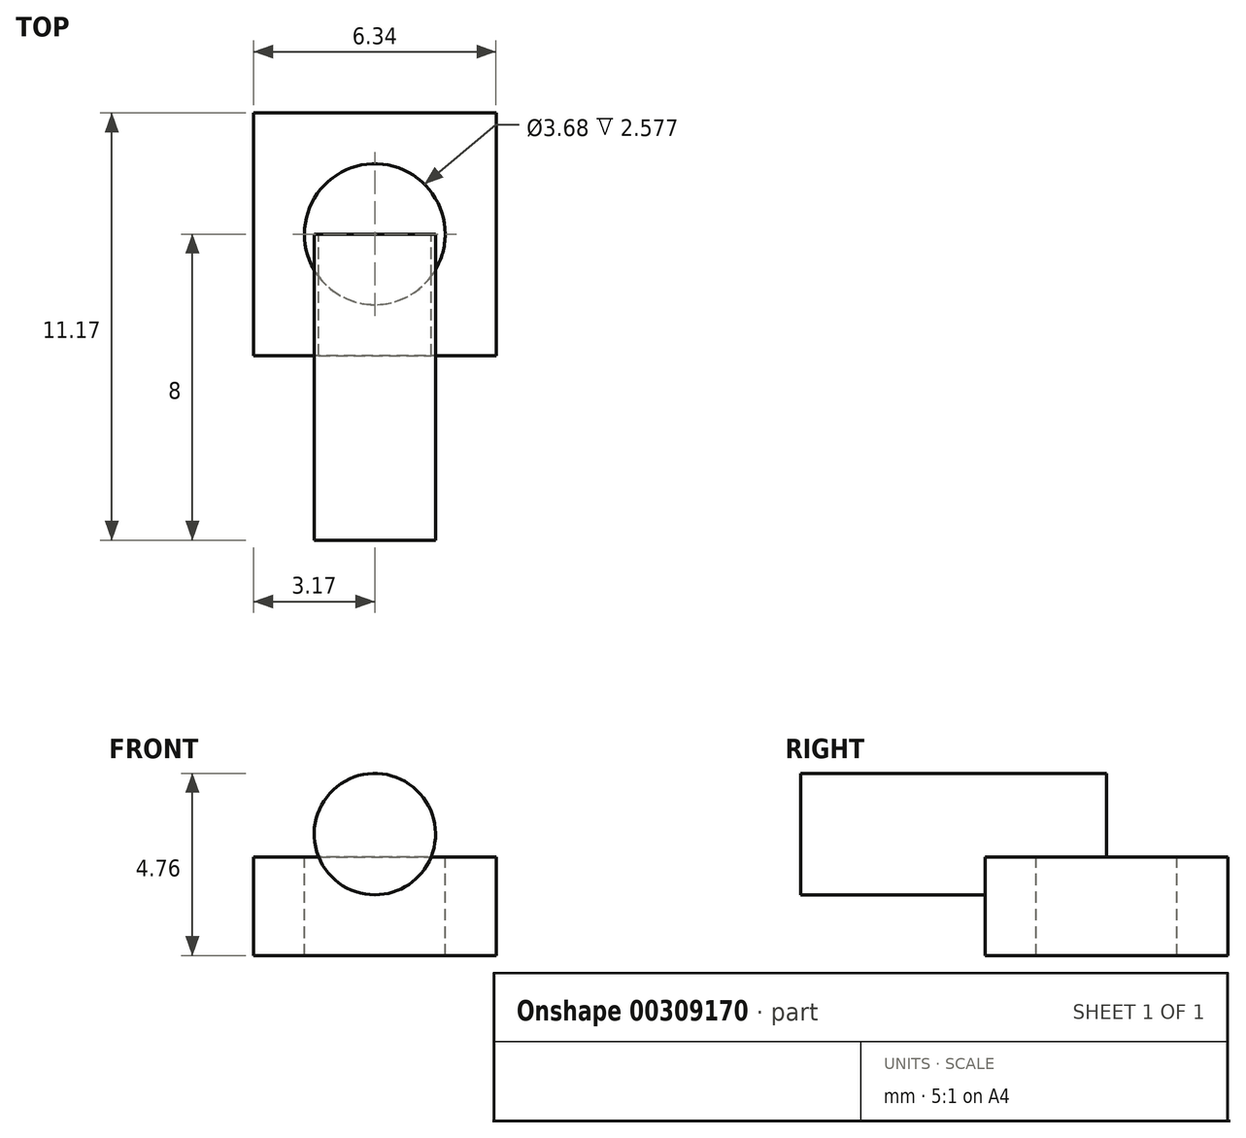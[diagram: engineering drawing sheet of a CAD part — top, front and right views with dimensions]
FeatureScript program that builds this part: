
annotation { "Feature Type Name" : "Feature", "Feature Type Description" : "" }
export const myFeature = defineFeature(function(context is Context, id is Id, definition is map)
    precondition{}
    {
        {
            var Q0;
            Q0=qCreatedBy(makeId("Front.planeOp"),FACE);
            var sketch = newSketch(context, id + "F0", { "sketchPlane" : qUnion([Q0])});
            skLineSegment(sketch, "E0", {"start": v(0, 0) * mm, "end": v(0, 3.18) * mm, "construction": true});
            skCircle(sketch, "E1", {"center": v(0, 3.18) * mm, "radius": 1.59 * mm});
            skSolve(sketch);
        }
        {
            var Q0;
            Q0=qCreatedBy(makeId("Top.planeOp"),FACE);
            var sketch = newSketch(context, id + "F1", { "sketchPlane" : qUnion([Q0])});
            skLineSegment(sketch, "E2.bottom", {"start": v(3.17, -3.18) * mm, "end": v(-3.18, -3.18) * mm});
            skLineSegment(sketch, "E2.top", {"start": v(3.17, 3.18) * mm, "end": v(-3.18, 3.18) * mm});
            skLineSegment(sketch, "E2.left", {"start": v(3.17, -3.18) * mm, "end": v(3.17, 3.17) * mm});
            skLineSegment(sketch, "E2.right", {"start": v(-3.18, -3.18) * mm, "end": v(-3.18, 3.17) * mm});
            skPoint(sketch, "E2.middle", {"position": v(0, 0) * mm});
            skCircle(sketch, "E3", {"center": v(0, 0) * mm, "radius": 1.59 * mm});
            skSolve(sketch);
        }
        {
            var Q0;
            Q0=makeQuery(id+"F1.imprint","IMPRINT",FACE,{"disambiguationData":[TD([[makeQuery(id+"F1.imprint","IMPRINT",EDGE,{"derivedFrom":sQuery(id+"F1.wireOp",EDGE,"E2.bottom")}),-1.0]])]});
            var Q1;
            Q1=makeQuery(id+"F1.imprint","IMPRINT",FACE,{"disambiguationData":[TD([[makeQuery(id+"F1.imprint","IMPRINT",EDGE,{"derivedFrom":sQuery(id+"F1.wireOp",EDGE,"E3")}),1.0]])]});
            extrude(context, id + "F2", {"entities" : qUnion([Q0, Q1]), "depth" : (50 / 24 / 3 + 0.62 + 17 / 24 + 0.6 * cos(45 * degree) + 0.12) * mm});
        }
        {
            var Q0;
            Q0=makeQuery(id+"F0.imprint","IMPRINT",FACE,{"disambiguationData":[TD([[makeQuery(id+"F0.imprint","IMPRINT",EDGE,{"derivedFrom":sQuery(id+"F0.wireOp",EDGE,"E1")}),1.0]])]});
            extrude(context, id + "F3", {"entities" : qUnion([Q0]), "operationType" : NewBodyOperationType.ADD, "depth" : 8 * mm});
        }
        {
            var Q0;
            Q0=makeQuery(id+"F2.opExtrude","CAP_FACE",FACE,{"disambiguationData":[OSD([sQuery(id+"F1.wireOp",EDGE,"E2.bottom"),sQuery(id+"F1.wireOp",EDGE,"E2.top"),sQuery(id+"F1.wireOp",EDGE,"E2.left"),sQuery(id+"F1.wireOp",EDGE,"E2.right")])],"isStart":false});
            var sketch = newSketch(context, id + "F4", { "sketchPlane" : qUnion([Q0])});
            skCircle(sketch, "E4", {"center": v(0, 0) * mm, "radius": 1.84 * mm});
            skSolve(sketch);
        }
        {
            var Q0;
            Q0 = qSketchRegion(id + "F4", true);
            extrude(context, id + "F5", {"entities" : qUnion([Q0]), "operationType" : NewBodyOperationType.REMOVE, "oppositeDirection" : true, "depth" : 3.17 * mm});
        }
    });
